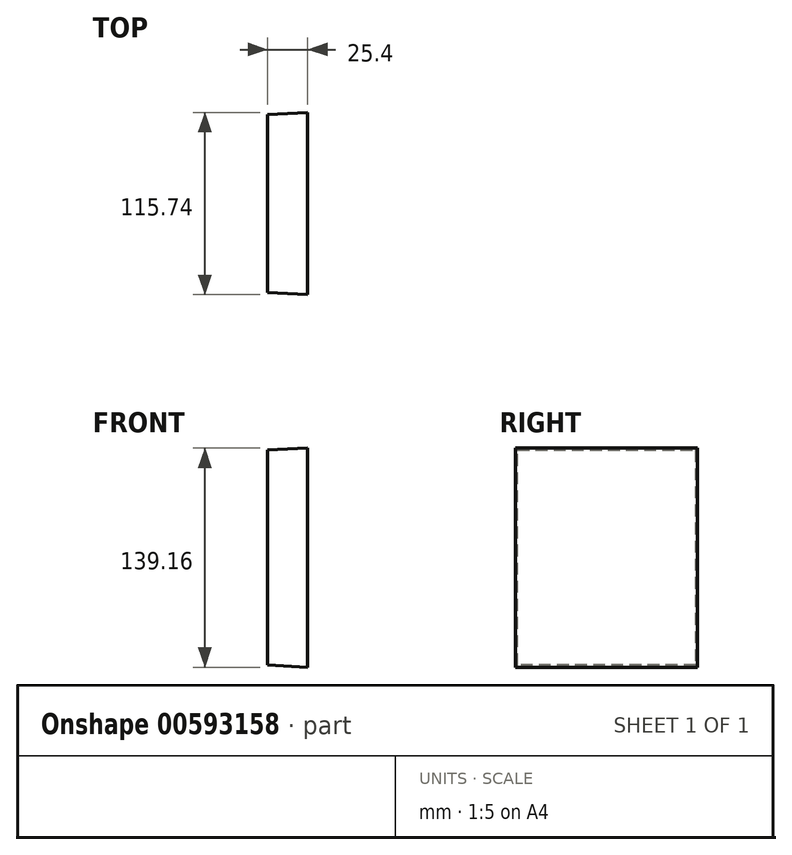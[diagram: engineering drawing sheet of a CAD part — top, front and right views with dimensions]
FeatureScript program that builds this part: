
annotation { "Feature Type Name" : "Feature", "Feature Type Description" : "" }
export const myFeature = defineFeature(function(context is Context, id is Id, definition is map)
    precondition{}
    {
        {
            var Q0;
            Q0=qCreatedBy(makeId("Right.planeOp"),FACE);
            var sketch = newSketch(context, id + "F0", { "sketchPlane" : qUnion([Q0])});
            skLineSegment(sketch, "E0.bottom", {"start": v(113.08, -66.78) * mm, "end": v(0, -66.78) * mm});
            skLineSegment(sketch, "E0.top", {"start": v(113.08, 69.72) * mm, "end": v(0, 69.72) * mm});
            skLineSegment(sketch, "E0.left", {"start": v(113.08, -66.78) * mm, "end": v(113.08, 69.72) * mm});
            skLineSegment(sketch, "E0.right", {"start": v(0, -66.78) * mm, "end": v(0, 69.72) * mm});
            skSolve(sketch);
        }
        {
            var Q0;
            Q0=makeQuery(id+"F0.imprint","IMPRINT",FACE,{"disambiguationData":[TD([[makeQuery(id+"F0.imprint","IMPRINT",EDGE,{"derivedFrom":sQuery(id+"F0.wireOp",EDGE,"E0.bottom")}),-1.0]])]});
            extrude(context, id + "F1", {"entities" : qUnion([Q0]), "depth" : 25.4 * mm, "offsetDistance" : 25.4 * mm, "hasDraft" : true, "draftAngle" : 3 * degree});
        }
    });
